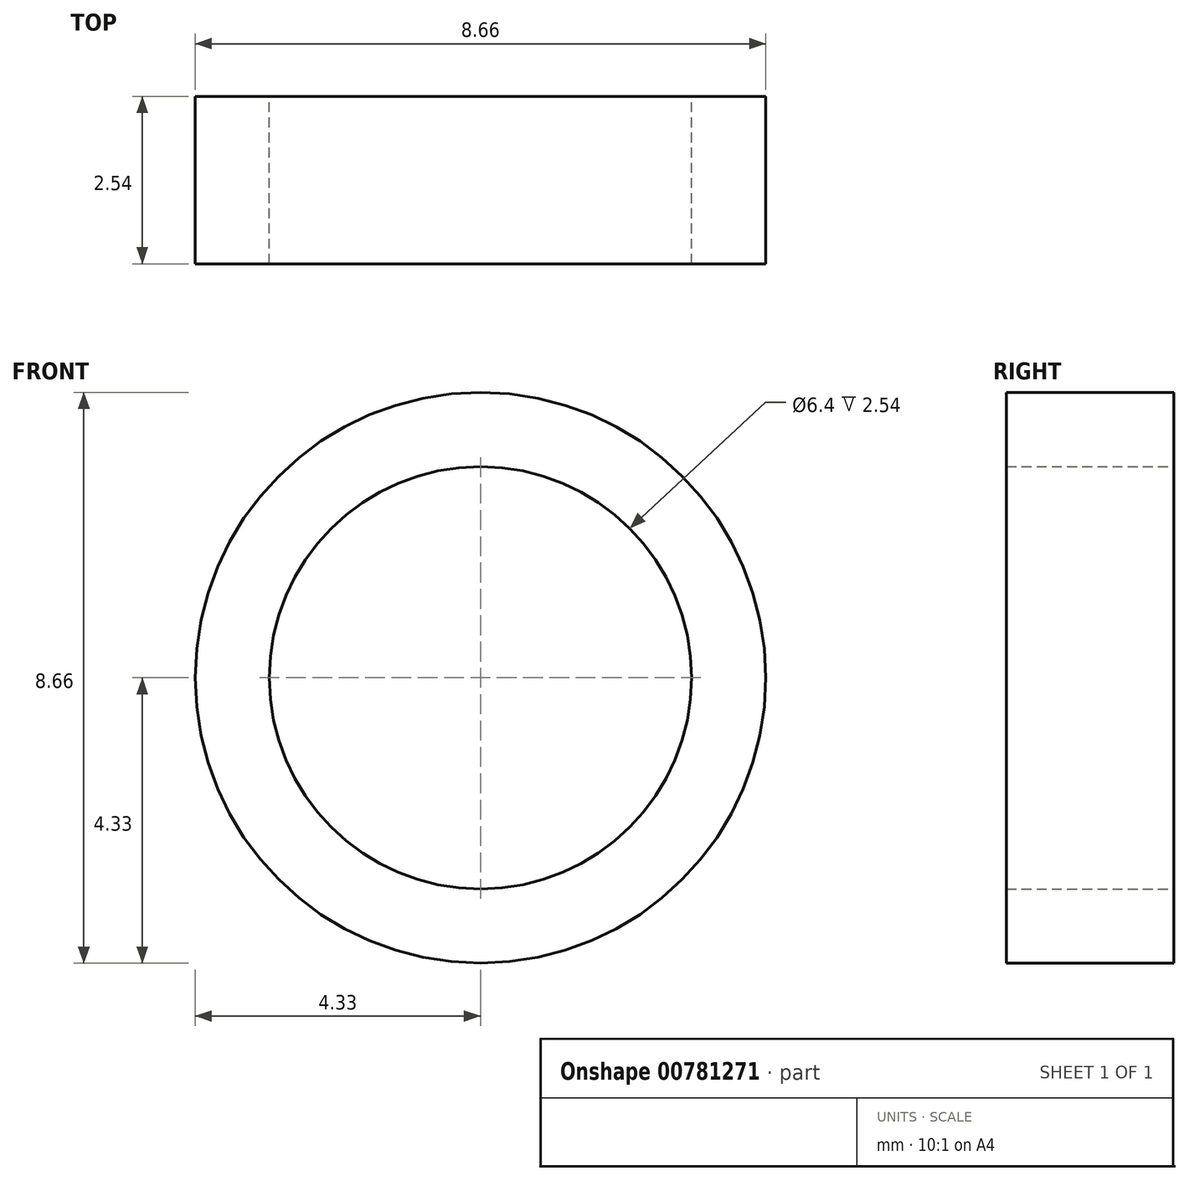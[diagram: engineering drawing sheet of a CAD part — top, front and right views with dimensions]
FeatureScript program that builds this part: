
annotation { "Feature Type Name" : "Feature", "Feature Type Description" : "" }
export const myFeature = defineFeature(function(context is Context, id is Id, definition is map)
    precondition{}
    {
        {
            var Q0;
            Q0=qCreatedBy(makeId("Front.planeOp"),FACE);
            var sketch = newSketch(context, id + "F0", { "sketchPlane" : qUnion([Q0])});
            skCircle(sketch, "E0", {"center": v(0, 0) * mm, "radius": 3.2 * mm});
            skCircle(sketch, "E1", {"center": v(0, 0) * mm, "radius": 4.33 * mm});
            skSolve(sketch);
        }
        {
            var Q0;
            Q0=qCreatedBy(makeId("Top.planeOp"),FACE);
            var sketch = newSketch(context, id + "F1", { "sketchPlane" : qUnion([Q0])});
            skFitSpline(sketch, "E2", {"points": [v(0, 0) * mm, v(2.16, 5.8) * mm, v(9.2, 8.98) * mm, v(17.62, 11.02) * mm, v(24.89, 11.93) * mm], "startDerivative": vector(5.13, 28.47) * mm, "endDerivative": vector(28.93, 2.76) * mm});
            skFitSpline(sketch, "E3", {"points": [v(0, 0) * mm, v(2.16, -6.7) * mm, v(11.25, -9.89) * mm, v(22.62, -11.7) * mm, v(31.48, -12.62) * mm, v(40.57, -15.57) * mm, v(46.03, -21.7) * mm], "startDerivative": vector(5.87, -51.98) * mm, "endDerivative": vector(29.52, -43.4) * mm});
            skSolve(sketch);
        }
        {
            var Q0;
            Q0=makeQuery(id+"F0.imprint","IMPRINT",FACE,{"disambiguationData":[TD([[makeQuery(id+"F0.imprint","IMPRINT",EDGE,{"derivedFrom":sQuery(id+"F0.wireOp",EDGE,"E0")}),-1.0]])]});
            var Q1;
            Q1=sQuery(id+"F0.wireOp",EDGE,"E1");
            var Q2;
            Q2=sQuery(id+"F0.wireOp",EDGE,"E0");
            extrude(context, id + "F2", {"entities" : qUnion([Q0]), "surfaceEntities" : qUnion([Q1, Q2]), "endBound" : BoundingType.SYMMETRIC, "depth" : 2.54 * mm, "offsetDistance" : 25.4 * mm});
        }
    });
